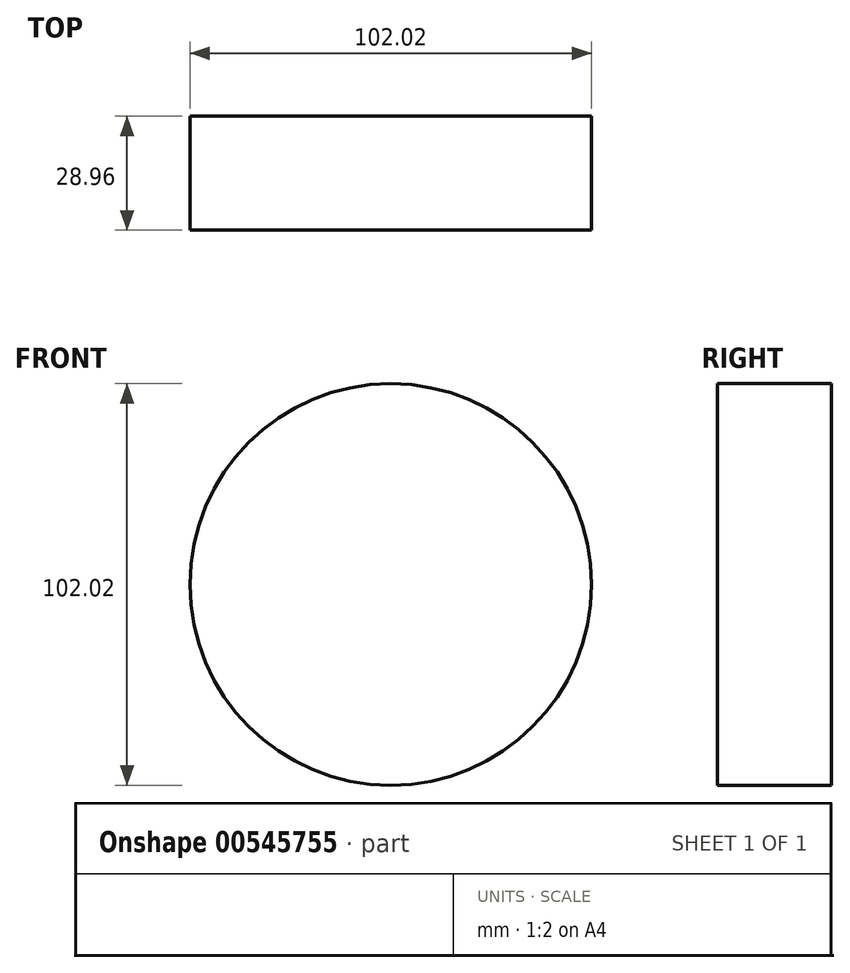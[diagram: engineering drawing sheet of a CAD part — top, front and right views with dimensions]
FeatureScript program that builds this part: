
annotation { "Feature Type Name" : "Feature", "Feature Type Description" : "" }
export const myFeature = defineFeature(function(context is Context, id is Id, definition is map)
    precondition{}
    {
        {
            var Q0;
            Q0=qCreatedBy(makeId("Front.planeOp"),FACE);
            var sketch = newSketch(context, id + "F0", { "sketchPlane" : qUnion([Q0])});
            skCircle(sketch, "E0", {"center": v(0, 0) * mm, "radius": 51 * mm});
            skSolve(sketch);
        }
        {
            var Q0;
            Q0=makeQuery(id+"F0.imprint","IMPRINT",FACE,{"disambiguationData":[TD([[makeQuery(id+"F0.imprint","IMPRINT",EDGE,{"derivedFrom":sQuery(id+"F0.wireOp",EDGE,"E0")}),1.0]])]});
            extrude(context, id + "F1", {"entities" : qUnion([Q0]), "depth" : 28.96 * mm, "offsetDistance" : 25.4 * mm});
        }
    });
